# Revit family: Haworth_XSeries_PersonalStorageTower_24Wide2HighFiles
name_source: partatom
category: Furniture Systems
units: mm (PartAtom-declared; Revit-internal decimal feet)

## family parameters
Always vertical = Yes
Cut with Voids When Loaded = No
OmniClass Number = 23.40.70.14.64.21
OmniClass Title = Systems Furniture
Part Type = Normal
Room Calculation Point = No
Round Connector Dimension = Use Diameter
Shared = No
Work Plane-Based = No

## types (4) — shared parameters
Actual Depth = 23 5/8"
Actual Width = 24"
Assembly Code = E2020200
Cabinet Height = 27 1/2"
Classic Pull = No
Crescent Pull = No
Description = Haworth XSeries Personal Storage Tower
Door Height = 24 1/8"
Door Width = 9"
Drawer 1 Height = 12"
Drawer 3 Height = 5 15/16"
Drawer Width = 14 7/8"
Ellipse Pull = No
J Pull = No
Linear Pull = Yes
Manufacturer = Haworth
Max. Height = 63 1/2"
Max. Width = 47 7/8"
Min. Height = 27 1/2"
Min. Width = 29 7/8"
Model = J2NB
Pull Finish = Haworth _ Metal _ Brushed Aluminum
Pull Height Centerline = 12 1/16"
Radius Pull = No
Revision Number = 4
Size = Verify Final Dim. w/ Haworth
Sustainability Info = https://www.haworth.com
Taper Pull = No
URL = http://www.haworth.com
URL - Product = https://www.haworth.com
Warranty = https://cdn.shopify.com

## per-type parameters (varying)
| type | Actual Height | Box Box File | Casters | Drawer 2 Height | Drawer 3 | File File |
| 24d 24w 27h - Valet Box Box File | 27 1/2" | Yes | No | 5 15/16" | Yes | No |
| 24d 24w 27h - Valet File File | 27 1/2" | No | No | 12" | No | Yes |
| 24d 24w 30h - Valet Box Box File - Mobile | 30 1/2" | Yes | Yes | 5 15/16" | Yes | No |
| 24d 24w 30h - Valet File File - Mobile | 30 1/2" | No | Yes | 12" | No | Yes |

## geometry (parser evidence)
native form markers: Sweep x16
no freeform markers — native parametric forms only
